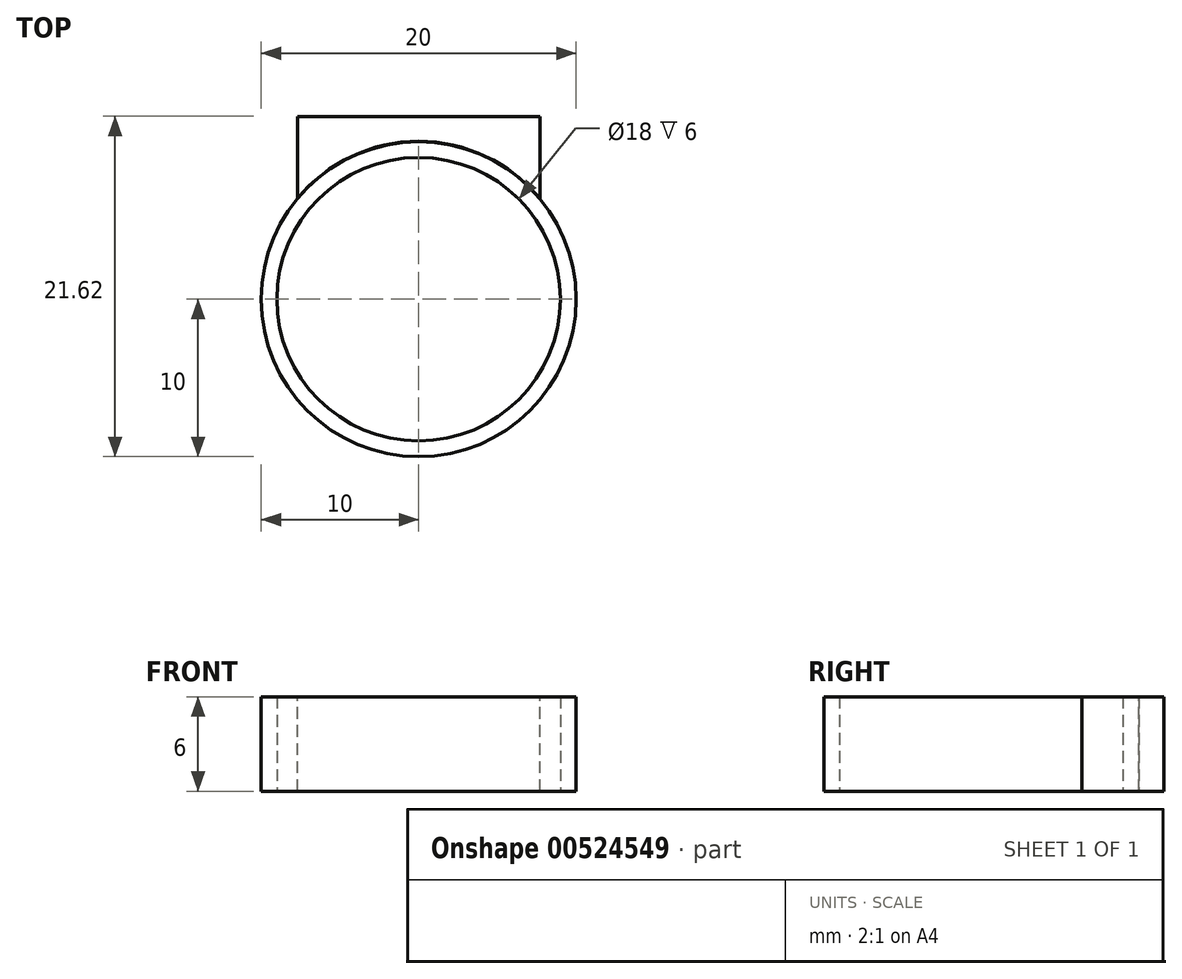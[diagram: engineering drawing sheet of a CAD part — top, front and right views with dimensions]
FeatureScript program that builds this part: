
annotation { "Feature Type Name" : "Feature", "Feature Type Description" : "" }
export const myFeature = defineFeature(function(context is Context, id is Id, definition is map)
    precondition{}
    {
        {
            var Q0;
            Q0=qCreatedBy(makeId("Top.planeOp"),FACE);
            var sketch = newSketch(context, id + "F0", { "sketchPlane" : qUnion([Q0])});
            skCircle(sketch, "E0", {"center": v(0, 0) * mm, "radius": 9 * mm});
            skCircle(sketch, "E1", {"center": v(0, 0) * mm, "radius": 10 * mm});
            skPoint(sketch, "E2.middle", {"position": v(0, 9) * mm});
            skSolve(sketch);
        }
        {
            var Q0;
            Q0 = qSketchRegion(id + "F0", true);
            extrude(context, id + "F1", {"entities" : qUnion([Q0]), "depth" : 6 * mm, "offsetDistance" : 25.4 * mm});
        }
        {
            var Q0;
            Q0=makeQuery(id+"F1.opExtrude","CAP_FACE",FACE,{"disambiguationData":[OSD([sQuery(id+"F0.wireOp",EDGE,"E0"),sQuery(id+"F0.wireOp",EDGE,"E1")])],"isStart":false});
            var sketch = newSketch(context, id + "F2", { "sketchPlane" : qUnion([Q0])});
            skLineSegment(sketch, "E3.top", {"start": v(7.7, 11.62) * mm, "end": v(-7.7, 11.62) * mm});
            skLineSegment(sketch, "E3.left", {"start": v(7.7, 6.38) * mm, "end": v(7.7, 11.62) * mm});
            skLineSegment(sketch, "E3.right", {"start": v(-7.7, 6.38) * mm, "end": v(-7.7, 11.62) * mm});
            skPoint(sketch, "E3.middle", {"position": v(0, 9) * mm});
            skArc(sketch, "E4", {"start": v(7.7, 6.38) * mm, "mid": v(0, 10.03) * mm, "end": v(-7.7, 6.38) * mm});
            skSolve(sketch);
        }
        {
            var Q0;
            Q0 = qSketchRegion(id + "F2", true);
            extrude(context, id + "F3", {"entities" : qUnion([Q0]), "oppositeDirection" : true, "depth" : 6 * mm, "offsetDistance" : 25.4 * mm});
        }
    });
